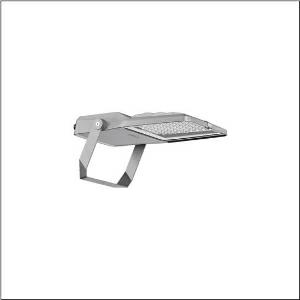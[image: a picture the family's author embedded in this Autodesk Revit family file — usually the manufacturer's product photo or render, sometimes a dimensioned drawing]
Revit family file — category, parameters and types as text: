
# Revit family: floodlight_fl_21_mini___pl33t_5xa7776d2f1a_88fb
name_source: partatom
category: Lighting Fixtures
units: mm (PartAtom-declared; Revit-internal decimal feet)

## family parameters
Cut with Voids When Loaded = No
Host = Face
Light Source = No
Part Type = Normal
Room Calculation Point = No
Round Connector Dimension = Use Diameter
Shared = No

## types (1)
- --- (1 x LED, 17630 lm, 142.9 W, 3000K)
    Apparent Load = 143 VA
    CIE Flux Codes = 26 75 99 100 100
    Color Rendering = 70
    Color Temperature = 3000K
    Default Elevation = 1800 mm
    Description = Floodlight FL 21 mini, floodlight, primary light control with lens, of PMMA, primary optical cover: protective disc, of toughened safety glass, transparent, light distribution: PL33T, light emission: direct distribution, installation type: surface-mounted, LED, High Power LED, rated luminous flux: 17.630lm, luminous efficacy: 123lm/W, light colour: 730, colour temperature: 3000K, control gear: Smart Interface (Zhaga), control: flexible luminous flux parameterisation, time-dependent luminous flux control, constant luminous flux control, overheat protection, pre-setting: logarithmic dimming characteristic, with terminal, 6-pole, mains connection: 220..240V, AC, 50/60Hz, start of lifetime: 143W, end of service life: 151W, reduction: 63W, luminaire housing, of diecast aluminium, powder-coated, Siteco® metallic grey (DB 702S), corrosivity category C5 mid according to DIN EN ISO 12944, suitable for swimming pools, chlorine-resistant, sealing non-destructively replaceable, mounting bracket, of steel, galvanised, powder-coated, Siteco® metallic grey (DB 702S), Smart Interface below and above, protection rating (complete): IP66, insulation class (complete): insulation class II (safety insulation), certification: CE, ENEC, VDE, protection symbol: D, impact resistance: IK08, permissible operating ambient temperature: -40..+40°C, permissible operating ambient temperature for outdoor applications: -40..+50°C, standard: DIN EN 12944, LABS conformity tested according to VDMA 24364:2018-05, packaging unit: 1 piece

Light Distribution: PL33T
    Height = 70 mm
    Lamp = 1 x LED
    Lamp Light Flux = 17630 lm
    Lamp Power = 142.9 W
    Lamp count = 1
    Length = 485 mm
    Luminous efficacy = 123 lm/W
    Manufacturer = Siteco
    ModVariant = No
    Model = 5XA7776D2F1A
    Number of Poles = 1
    OnlyDefault = Yes
    Power Factor = 1
    Product Name = Floodlight FL 21 mini | PL33T
    Product group = floodlight | pylon annexe
    ProductGroupID = 6200
    Protection Class = Protection class II
    Protection Degree = IP 66
    RLX_Detail_Level = 1
    RLX_Emergency_Light_Flux = 0 lm
    RLX_Emergency_Type = 0
    RLX_Emergency_Type_DB = No
    RlxData = <blob elided: 96205 chars, md5=e9e45ba6>
    Socket = socket
    Standby Power = 0 W
    System Light Flux = 17630 lm
    System Power = 143 W
    Type Comments = factory setting: luminous flux: 100 % | dim-lin: 254 | 730 mA
    Type Image = l_1006845.jpg
    URL = http://relux.com
    VarID = @adj_148370
    Voltage = 0 V
    Weight = 0.00 kg
    Width = 337 mm

## geometry (parser evidence)
native form markers: Blend x4, Sweep x11
no freeform markers — native parametric forms only
